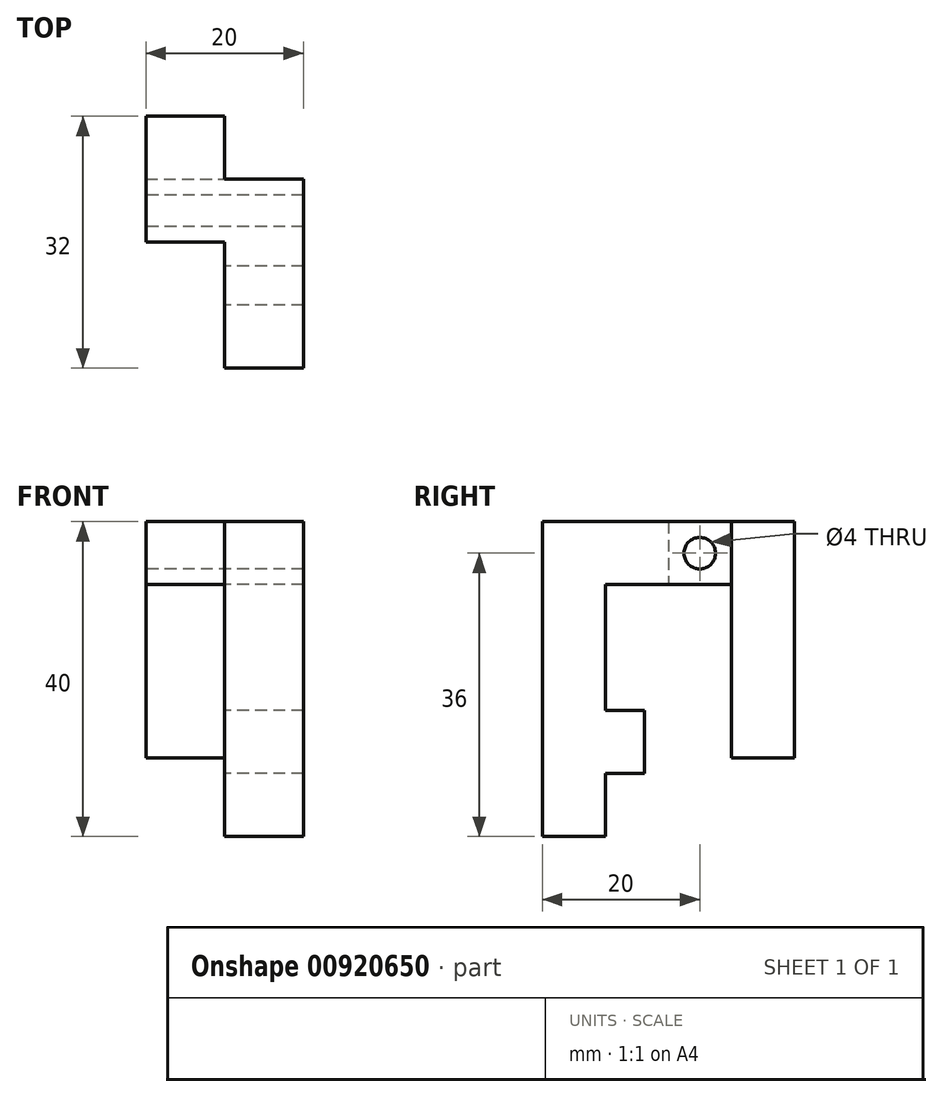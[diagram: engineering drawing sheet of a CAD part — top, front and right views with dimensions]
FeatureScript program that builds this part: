
annotation { "Feature Type Name" : "Feature", "Feature Type Description" : "" }
export const myFeature = defineFeature(function(context is Context, id is Id, definition is map)
    precondition{}
    {
        {
            var Q0;
            Q0=qCreatedBy(makeId("Right.planeOp"),FACE);
            var sketch = newSketch(context, id + "F0", { "sketchPlane" : qUnion([Q0])});
            skLineSegment(sketch, "E0.bottom", {"start": v(2.5, 4) * mm, "end": v(-2.5, 4) * mm});
            skLineSegment(sketch, "E0.top", {"start": v(2.5, -4) * mm, "end": v(-2.5, -4) * mm});
            skLineSegment(sketch, "E0.left", {"start": v(2.5, 4) * mm, "end": v(2.5, -4) * mm});
            skLineSegment(sketch, "E0.right", {"start": v(-2.5, 4) * mm, "end": v(-2.5, -4) * mm, "construction": true});
            skPoint(sketch, "E0.middle", {"position": v(0, 0) * mm});
            skLineSegment(sketch, "E1", {"start": v(-2.5, -4) * mm, "end": v(-2.5, -12) * mm});
            skLineSegment(sketch, "E2", {"start": v(-2.5, -12) * mm, "end": v(-10.5, -12) * mm});
            skLineSegment(sketch, "E3", {"start": v(-10.5, -12) * mm, "end": v(-10.5, 28) * mm});
            skLineSegment(sketch, "E4", {"start": v(-10.5, 28) * mm, "end": v(13.5, 28) * mm});
            skLineSegment(sketch, "E5", {"start": v(13.5, 28) * mm, "end": v(13.5, 20) * mm});
            skLineSegment(sketch, "E6", {"start": v(13.5, 20) * mm, "end": v(-2.5, 20) * mm});
            skLineSegment(sketch, "E7", {"start": v(-2.5, 20) * mm, "end": v(-2.5, 4) * mm});
            skCircle(sketch, "E8", {"center": v(9.5, 24) * mm, "radius": 2 * mm});
            skLineSegment(sketch, "E9", {"start": v(9.5, 28) * mm, "end": v(9.5, 20) * mm, "construction": true});
            skSolve(sketch);
        }
        {
            var Q0;
            Q0=makeQuery(id+"F0.imprint","IMPRINT",FACE,{"disambiguationData":[TD([[makeQuery(id+"F0.imprint","IMPRINT",EDGE,{"derivedFrom":sQuery(id+"F0.wireOp",EDGE,"E0.bottom")}),1.0]])]});
            extrude(context, id + "F1", {"entities" : qUnion([Q0]), "depth" : 10 * mm, "offsetDistance" : 25 * mm});
        }
        {
            var Q0;
            Q0=makeQuery(id+"F1.opExtrude","CAP_FACE",FACE,{"disambiguationData":[OSD([sQuery(id+"F0.wireOp",EDGE,"E0.bottom"),sQuery(id+"F0.wireOp",EDGE,"E0.top"),sQuery(id+"F0.wireOp",EDGE,"E0.left"),sQuery(id+"F0.wireOp",EDGE,"E1"),sQuery(id+"F0.wireOp",EDGE,"E2"),sQuery(id+"F0.wireOp",EDGE,"E3"),sQuery(id+"F0.wireOp",EDGE,"E4"),sQuery(id+"F0.wireOp",EDGE,"E5"),sQuery(id+"F0.wireOp",EDGE,"E6"),sQuery(id+"F0.wireOp",EDGE,"E7"),sQuery(id+"F0.wireOp",EDGE,"E8")])],"isStart":true});
            var sketch = newSketch(context, id + "F2", { "sketchPlane" : qUnion([Q0])});
            skLineSegment(sketch, "E10", {"start": v(-13.5, 20) * mm, "end": v(-13.5, -2) * mm});
            skLineSegment(sketch, "E11", {"start": v(-13.5, -2) * mm, "end": v(-21.5, -2) * mm});
            skLineSegment(sketch, "E12", {"start": v(-21.5, -2) * mm, "end": v(-21.5, 28) * mm});
            skLineSegment(sketch, "E13", {"start": v(-21.5, 28) * mm, "end": v(-13.5, 28) * mm});
            skLineSegment(sketch, "E14", {"start": v(-13.5, 28) * mm, "end": v(-13.5, 33) * mm});
            skLineSegment(sketch, "E15", {"start": v(-13.5, 33) * mm, "end": v(-5.5, 33) * mm});
            skLineSegment(sketch, "E16", {"start": v(-5.5, 33) * mm, "end": v(-5.5, 20) * mm});
            skLineSegment(sketch, "E17", {"start": v(-5.5, 20) * mm, "end": v(-13.5, 20) * mm});
            skCircle(sketch, "E18.0", {"center": v(-9.5, 24) * mm, "radius": 2 * mm});
            skSolve(sketch);
        }
        {
            var Q0;
            Q0=makeQuery(id+"F2.imprint","IMPRINT",FACE,{"disambiguationData":[TD([[makeQuery(id+"F2.imprint","IMPRINT",EDGE,{"derivedFrom":sQuery(id+"F2.wireOp",EDGE,"E10")}),-1.0]])]});
            var Q1;
            {var subQ4=sQuery(id+"F2.wireOp",EDGE,"E17");Q1=makeQuery(id+"F2.imprint","IMPRINT",FACE,{"disambiguationData":[TD([[makeQuery(id+"F2.imprint","IMPRINT",EDGE,{"derivedFrom":subQ4}),1.0]])]});}
            extrude(context, id + "F3", {"entities" : qUnion([Q0, Q1]), "operationType" : NewBodyOperationType.ADD, "depth" : 10 * mm, "offsetDistance" : 25 * mm});
        }
    });
